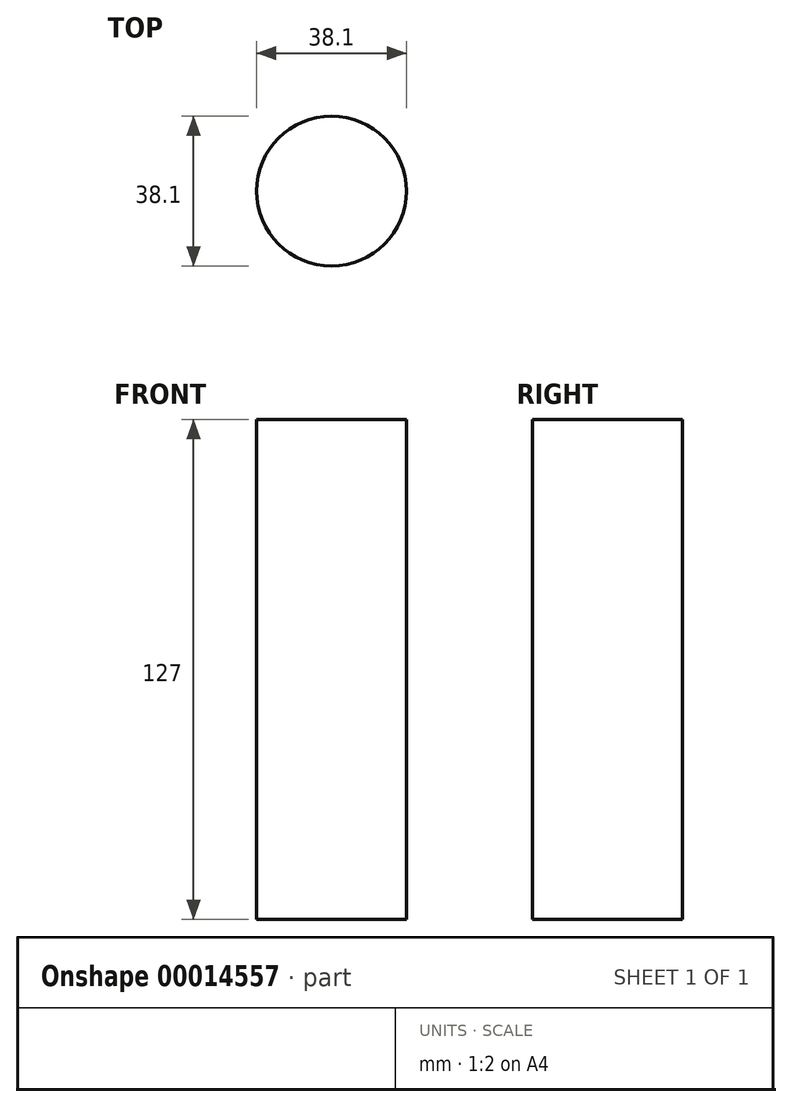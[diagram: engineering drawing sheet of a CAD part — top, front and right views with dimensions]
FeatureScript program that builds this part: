
annotation { "Feature Type Name" : "Feature", "Feature Type Description" : "" }
export const myFeature = defineFeature(function(context is Context, id is Id, definition is map)
    precondition{}
    {
        {
            var Q0;
            Q0=qCreatedBy(makeId("Top.planeOp"),FACE);
            var sketch = newSketch(context, id + "F0", { "sketchPlane" : qUnion([Q0])});
            skCircle(sketch, "E0", {"center": v(0, 0) * mm, "radius": 19.05 * mm});
            skSolve(sketch);
        }
        {
            var Q0;
            Q0=makeQuery(id+"F0.imprint","IMPRINT",FACE,{"disambiguationData":[TD([[makeQuery(id+"F0.imprint","IMPRINT",EDGE,{"derivedFrom":sQuery(id+"F0.wireOp",EDGE,"E0")}),1.0]])]});
            extrude(context, id + "F1", {"entities" : qUnion([Q0]), "endBound" : BoundingType.SYMMETRIC, "depth" : 127 * mm});
        }
    });
